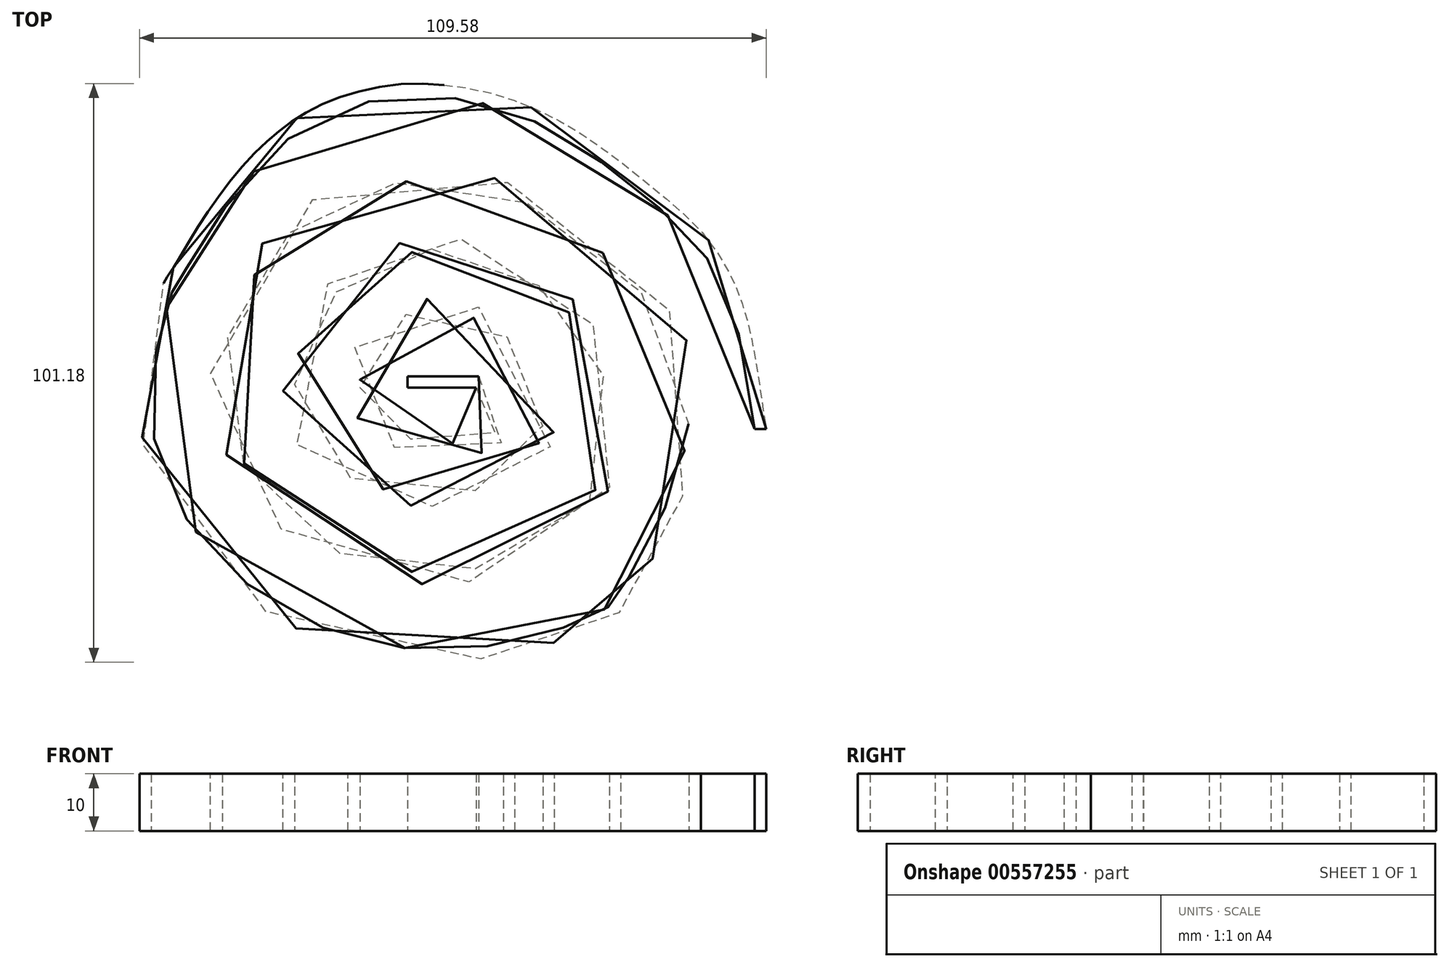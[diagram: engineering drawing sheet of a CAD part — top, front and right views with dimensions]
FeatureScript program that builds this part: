
annotation { "Feature Type Name" : "Feature", "Feature Type Description" : "" }
export const myFeature = defineFeature(function(context is Context, id is Id, definition is map)
    precondition{}
    {
        {
            var Q0;
            Q0=qCreatedBy(makeId("Top.planeOp"),FACE);
            var sketch = newSketch(context, id + "F0", { "sketchPlane" : qUnion([Q0])});
            skLineSegment(sketch, "E0.bottom", {"start": v(-6, 0) * mm, "end": v(6, 0) * mm});
            skLineSegment(sketch, "E0.top", {"start": v(-6, 2) * mm, "end": v(6, 2) * mm});
            skLineSegment(sketch, "E0.left", {"start": v(-6, 0) * mm, "end": v(-6, 2) * mm});
            skFitSpline(sketch, "E1", {"points": [v(6, 0) * mm, v(10.35, -2.27) * mm, v(8.9, -8.24) * mm, v(-1.8, -9.47) * mm, v(-11.05, -6.8) * mm, v(-14.34, 2) * mm, v(-7.96, 12.12) * mm, v(8.08, 11.1) * mm, v(16.93, 0) * mm, v(15.08, -13.18) * mm, v(-2, -18.73) * mm, v(-22.16, -11.12) * mm, v(-24.83, 7.19) * mm, v(-15.98, 18.7) * mm, v(0, 24.26) * mm, v(17.96, 17.06) * mm, v(28.24, 2) * mm, v(24.74, -21.4) * mm, v(0, -32.3) * mm, v(-25.24, -24.5) * mm, v(-38.2, -2.48) * mm, v(-32.65, 19.94) * mm, v(-17.42, 33.1) * mm, v(6, 35.37) * mm, v(31.94, 19.94) * mm, v(43.05, -7.21) * mm, v(31.33, -35.4) * mm, v(28.24, -38.9) * mm, v(6, -45.47) * mm, v(-27.92, -38.48) * mm, v(-50.34, -9.06) * mm, v(-47.05, 17.06) * mm, v(-45.4, 19.74) * mm, v(-26.27, 44) * mm, v(9.32, 49.15) * mm, v(35.24, 33.72) * mm, v(51.08, 12.54) * mm, v(57.92, -15.65) * mm], "startDerivative": vector(402.91, -94.3) * mm, "endDerivative": vector(314.93, -17.42) * mm});
            skFitSpline(sketch, "E2.0", {"points": [v(6.46, 1.95) * mm, v(6.98, 1.82) * mm, v(7.82, 1.63) * mm, v(8.99, 1.25) * mm, v(9.87, 0.86) * mm, v(10.75, 0.32) * mm, v(11.43, -0.31) * mm, v(11.9, -0.94) * mm, v(12.2, -1.46) * mm, v(12.41, -2.01) * mm, v(12.62, -2.76) * mm, v(12.75, -3.7) * mm, v(12.7, -4.85) * mm, v(12.5, -6) * mm, v(12.12, -7.12) * mm, v(11.57, -8.2) * mm, v(10.95, -9.04) * mm, v(10.35, -9.65) * mm, v(9.67, -10.2) * mm, v(8.77, -10.75) * mm, v(7.61, -11.2) * mm, v(6.42, -11.5) * mm, v(5.2, -11.7) * mm, v(3.55, -11.8) * mm, v(1.88, -11.78) * mm, v(0.23, -11.67) * mm, v(-0.78, -11.58) * mm, v(-1.57, -11.5) * mm, v(-2.35, -11.43) * mm, v(-3.7, -11.3) * mm, v(-5.58, -11.06) * mm, v(-7.78, -10.62) * mm, v(-9.55, -10.03) * mm, v(-10.9, -9.36) * mm, v(-11.86, -8.74) * mm, v(-12.76, -7.98) * mm, v(-13.56, -7.13) * mm, v(-14.27, -6.19) * mm, v(-15.07, -4.83) * mm, v(-15.84, -2.96) * mm, v(-16.34, -0.53) * mm, v(-16.4, 1.6) * mm, v(-16.22, 3.31) * mm, v(-15.89, 5.02) * mm, v(-15.2, 7.12) * mm, v(-13.91, 9.49) * mm, v(-12.19, 11.6) * mm, v(-10.38, 13.08) * mm, v(-8.71, 14.02) * mm, v(-7.38, 14.57) * mm, v(-6, 14.99) * mm, v(-4.08, 15.37) * mm, v(-1.62, 15.55) * mm, v(1.39, 15.34) * mm, v(4.36, 14.74) * mm, v(7.2, 13.78) * mm, v(10.74, 12.04) * mm, v(14.4, 9.1) * mm, v(17.01, 5.35) * mm, v(18.45, 2.01) * mm, v(19.2, -0.62) * mm, v(19.63, -3.36) * mm, v(19.69, -6.13) * mm, v(19.33, -8.88) * mm, v(18.64, -11.07) * mm, v(17.82, -12.73) * mm, v(17.07, -13.91) * mm, v(16.17, -15.01) * mm, v(15.14, -16) * mm, v(14.01, -16.86) * mm, v(12.39, -17.89) * mm, v(10.15, -18.92) * mm, v(7.22, -19.82) * mm, v(4.1, -20.41) * mm, v(0.83, -20.72) * mm, v(-2.52, -20.76) * mm, v(-5.92, -20.56) * mm, v(-9.3, -20.08) * mm, v(-12.6, -19.3) * mm, v(-15.75, -18.21) * mm, v(-18.7, -16.76) * mm, v(-20.9, -15.23) * mm, v(-22.5, -13.78) * mm, v(-23.58, -12.6) * mm, v(-24.53, -11.29) * mm, v(-25.62, -9.45) * mm, v(-26.66, -6.99) * mm, v(-27.44, -3.88) * mm, v(-27.79, -0.7) * mm, v(-27.74, 3.5) * mm, v(-26.78, 8.51) * mm, v(-24.75, 12.67) * mm, v(-22.6, 15.52) * mm, v(-20.76, 17.45) * mm, v(-19.08, 18.9) * mm, v(-17.65, 19.98) * mm, v(-16.17, 21.02) * mm, v(-14.22, 22.26) * mm, v(-11.7, 23.58) * mm, v(-9.06, 24.7) * mm, v(-6.28, 25.56) * mm, v(-3.38, 26.13) * mm, v(-0.9, 26.3) * mm, v(1.12, 26.23) * mm, v(3.13, 26.03) * mm, v(5.62, 25.55) * mm, v(8.56, 24.65) * mm, v(11.42, 23.47) * mm, v(14.16, 22.05) * mm, v(16.77, 20.43) * mm, v(19.22, 18.66) * mm, v(21.49, 16.75) * mm, v(23.57, 14.69) * mm, v(25.44, 12.45) * mm, v(27.09, 10.01) * mm, v(28.5, 7.38) * mm, v(29.63, 4.53) * mm, v(30.49, 1.46) * mm, v(31.06, -1.81) * mm, v(31.31, -5.22) * mm, v(31.23, -8.7) * mm, v(30.79, -12.18) * mm, v(29.94, -15.6) * mm, v(28.67, -18.88) * mm, v(27.22, -21.45) * mm, v(25.8, -23.35) * mm, v(24.23, -25.12) * mm, v(22.02, -27.1) * mm, v(19.03, -29.13) * mm, v(15.78, -30.8) * mm, v(11.18, -32.6) * mm, v(6.29, -33.74) * mm, v(1.34, -34.29) * mm, v(-2.33, -34.4) * mm, v(-5.95, -34.2) * mm, v(-10.68, -33.55) * mm, v(-16.37, -32) * mm, v(-21.63, -29.46) * mm, v(-25.52, -26.87) * mm, v(-28.26, -24.63) * mm, v(-30.78, -22.14) * mm, v(-33.84, -18.52) * mm, v(-36.38, -14.52) * mm, v(-38.3, -10.24) * mm, v(-39.4, -6.93) * mm, v(-40.01, -4.1) * mm, v(-40.3, -1.83) * mm, v(-40.46, 0.45) * mm, v(-40.42, 3.29) * mm, v(-39.88, 7.76) * mm, v(-38.42, 13.16) * mm, v(-36.11, 18.14) * mm, v(-33.89, 21.78) * mm, v(-31.43, 25.16) * mm, v(-27.93, 28.9) * mm, v(-23.04, 32.6) * mm, v(-17.51, 35.43) * mm, v(-11.39, 37.4) * mm, v(-5.93, 38.2) * mm, v(-1.42, 38.3) * mm, v(2.01, 38.1) * mm, v(5.46, 37.58) * mm, v(8.92, 36.74) * mm, v(12.34, 35.6) * mm, v(16.83, 33.7) * mm, v(22.26, 30.7) * mm, v(27.35, 26.95) * mm, v(31.14, 23.6) * mm, v(33.82, 20.93) * mm, v(36.33, 18.1) * mm, v(39.4, 14.12) * mm, v(42.57, 8.73) * mm, v(44.56, 2.78) * mm, v(45.24, -2.3) * mm, v(45.24, -5.59) * mm, v(44.96, -8.29) * mm, v(44.5, -11) * mm, v(43.65, -14.4) * mm, v(42.28, -18.42) * mm, v(40.67, -22.3) * mm, v(38.94, -25.95) * mm, v(37.18, -29.3) * mm, v(35.8, -31.78) * mm, v(34.78, -33.53) * mm, v(34.08, -34.7) * mm, v(33.56, -35.57) * mm, v(33.19, -36.18) * mm, v(32.85, -36.74) * mm, v(32.48, -37.36) * mm, v(32.05, -38.03) * mm, v(31.58, -38.67) * mm, v(31.04, -39.28) * mm, v(30.4, -39.84) * mm, v(29.7, -40.35) * mm, v(28.9, -40.83) * mm, v(27.98, -41.32) * mm, v(26.94, -41.83) * mm, v(25.38, -42.53) * mm, v(23.15, -43.41) * mm, v(20.08, -44.47) * mm, v(16.7, -45.46) * mm, v(13.05, -46.35) * mm, v(9.24, -47.08) * mm, v(4.03, -47.77) * mm, v(-2.53, -47.98) * mm, v(-10.38, -47.17) * mm, v(-16.8, -45.58) * mm, v(-21.83, -43.75) * mm, v(-25.53, -42.09) * mm, v(-29.14, -40.14) * mm, v(-33.82, -37.15) * mm, v(-39.3, -32.73) * mm, v(-44.05, -27.49) * mm, v(-47.23, -22.84) * mm, v(-49.25, -19.15) * mm, v(-50.88, -15.26) * mm, v(-51.85, -11.87) * mm, v(-52.38, -9.08) * mm, v(-52.74, -6.25) * mm, v(-52.89, -2.7) * mm, v(-52.7, 1.46) * mm, v(-52.21, 5.43) * mm, v(-51.53, 9.1) * mm, v(-50.75, 12.37) * mm, v(-49.93, 15.13) * mm, v(-49.28, 16.92) * mm, v(-48.82, 18.01) * mm, v(-48.5, 18.68) * mm, v(-48.16, 19.25) * mm, v(-47.84, 19.72) * mm, v(-47.55, 20.13) * mm, v(-47.28, 20.51) * mm, v(-47.03, 20.9) * mm, v(-46.82, 21.23) * mm, v(-46.58, 21.63) * mm, v(-46.22, 22.21) * mm, v(-45.72, 23.06) * mm, v(-44.79, 24.61) * mm, v(-43.4, 26.89) * mm, v(-41.42, 30) * mm, v(-39.12, 33.33) * mm, v(-36.52, 36.74) * mm, v(-33.63, 40.1) * mm, v(-30.97, 42.74) * mm, v(-28.7, 44.68) * mm, v(-26.34, 46.48) * mm, v(-23.24, 48.4) * mm, v(-19.34, 50.22) * mm, v(-15.3, 51.58) * mm, v(-9.82, 52.8) * mm, v(-4.25, 53.18) * mm, v(1.23, 52.84) * mm, v(5.26, 52.25) * mm, v(9.16, 51.33) * mm, v(12.9, 50.13) * mm, v(16.44, 48.67) * mm, v(20.95, 46.44) * mm, v(25.14, 43.86) * mm, v(29.05, 41.11) * mm, v(31.86, 39) * mm, v(34.1, 37.22) * mm, v(35.84, 35.81) * mm, v(37.55, 34.42) * mm, v(39.65, 32.69) * mm, v(42.9, 29.8) * mm, v(45.94, 26.64) * mm, v(48.64, 22.9) * mm, v(50.15, 20.29) * mm, v(51.23, 18) * mm, v(51.98, 16.17) * mm, v(52.66, 14.24) * mm, v(53.27, 12.18) * mm, v(53.8, 10.03) * mm, v(54.44, 7.06) * mm, v(55.11, 3.26) * mm, v(55.8, -1.27) * mm, v(56.3, -4.8) * mm, v(56.72, -7.37) * mm, v(57.03, -9.13) * mm, v(57.3, -10.43) * mm, v(57.53, -11.35) * mm, v(57.7, -11.98) * mm, v(57.88, -12.53) * mm, v(58.05, -13) * mm, v(58.2, -13.3) * mm, v(58.3, -13.5) * mm, v(58.36, -13.63) * mm, v(58.42, -13.72) * mm, v(58.46, -13.78) * mm, v(58.49, -13.8) * mm, v(58.5, -13.82) * mm, v(58.5, -13.82) * mm, v(58.5, -13.82) * mm, v(58.5, -13.82) * mm, v(58.5, -13.82) * mm, v(58.5, -13.82) * mm, v(58.5, -13.83) * mm, v(58.52, -13.83) * mm, v(58.53, -13.85) * mm, v(58.55, -13.86) * mm, v(58.57, -13.9) * mm, v(58.62, -13.93) * mm, v(58.67, -13.99) * mm, v(58.74, -14.05) * mm, v(58.83, -14.13) * mm, v(58.94, -14.24) * mm, v(59.07, -14.37) * mm, v(59.2, -14.5) * mm, v(59.38, -14.67) * mm, v(59.6, -14.88) * mm, v(59.86, -15.13) * mm, v(60.21, -15.47) * mm, v(60.65, -15.9) * mm, v(61, -16.24) * mm, v(61.18, -16.4) * mm]});
            skLineSegment(sketch, "E3", {"start": v(54.67, -7.21) * mm, "end": v(56.7, -7.21) * mm});
            skLineSegment(sketch, "E4", {"start": v(6, 2) * mm, "end": v(6.46, 1.95) * mm});
            skSolve(sketch);
        }
        {
            var Q0;
            Q0 = qSketchRegion(id + "F0", true);
            extrude(context, id + "F1", {"entities" : qUnion([Q0]), "depth" : 10 * mm, "offsetDistance" : 25 * mm});
        }
    });
